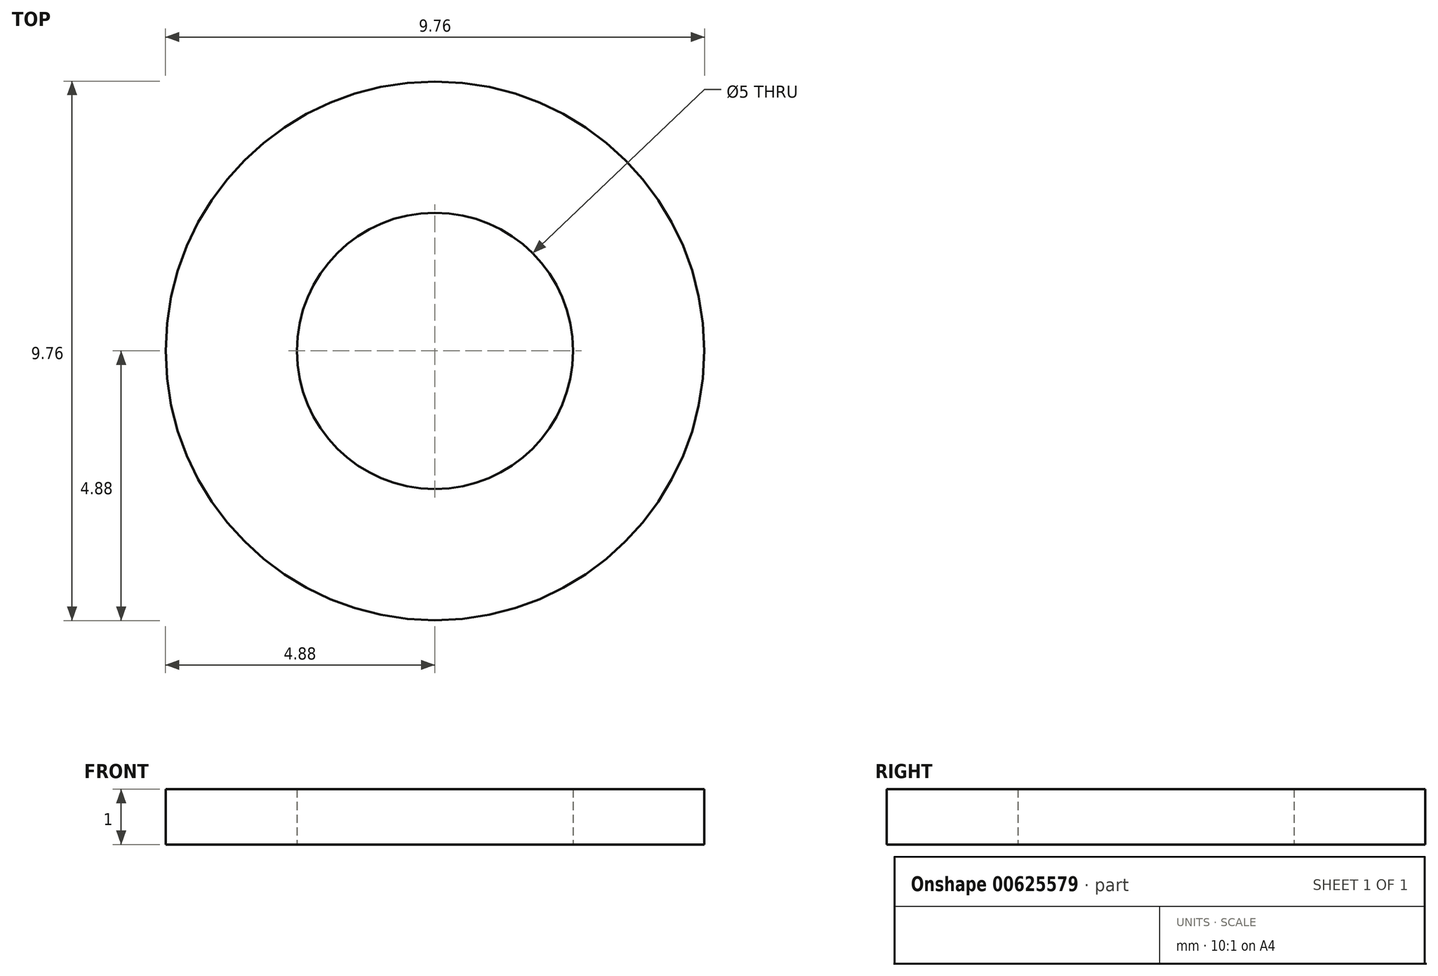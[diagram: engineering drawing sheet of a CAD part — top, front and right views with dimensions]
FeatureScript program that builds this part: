
annotation { "Feature Type Name" : "Feature", "Feature Type Description" : "" }
export const myFeature = defineFeature(function(context is Context, id is Id, definition is map)
    precondition{}
    {
        {
            var Q0;
            Q0=qCreatedBy(makeId("Top.planeOp"),FACE);
            var sketch = newSketch(context, id + "F0", { "sketchPlane" : qUnion([Q0])});
            skCircle(sketch, "E0", {"center": v(0, 0) * mm, "radius": 2.5 * mm});
            skCircle(sketch, "E1", {"center": v(0, 0) * mm, "radius": 4.88 * mm});
            skSolve(sketch);
        }
        {
            var Q0;
            Q0 = qSketchRegion(id + "F0", true);
            extrude(context, id + "F1", {"entities" : qUnion([Q0]), "depth" : 1 * mm, "offsetDistance" : 25 * mm});
        }
    });
